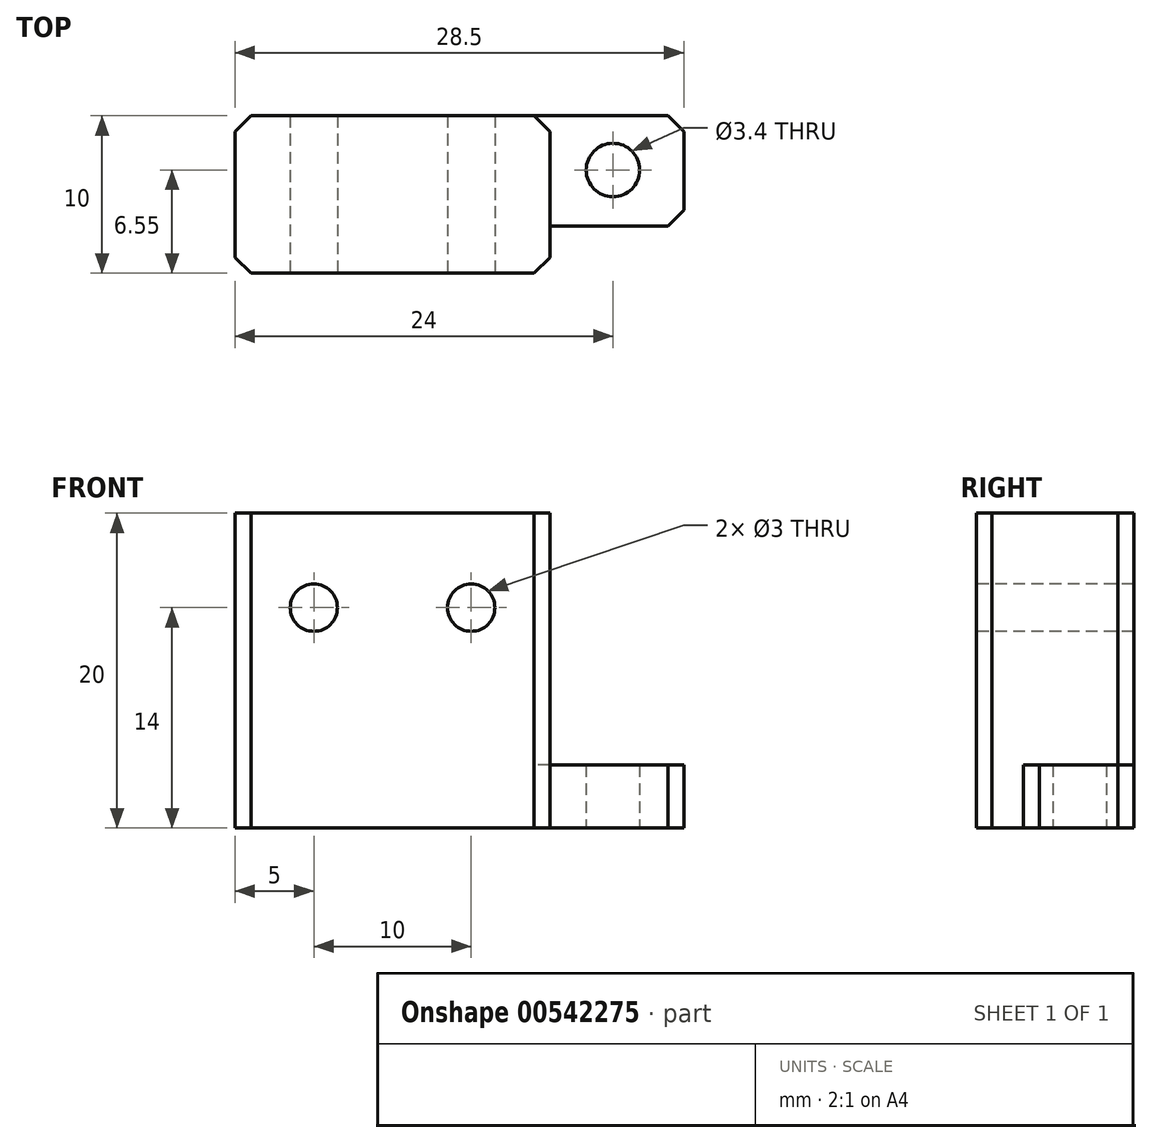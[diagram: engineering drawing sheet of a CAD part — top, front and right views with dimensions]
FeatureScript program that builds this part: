
annotation { "Feature Type Name" : "Feature", "Feature Type Description" : "" }
export const myFeature = defineFeature(function(context is Context, id is Id, definition is map)
    precondition{}
    {
        {
            var Q0;
            Q0=qCreatedBy(makeId("Top.planeOp"),FACE);
            var sketch = newSketch(context, id + "F0", { "sketchPlane" : qUnion([Q0])});
            skLineSegment(sketch, "E0.bottom", {"start": v(-8, 3.45) * mm, "end": v(-4, 3.45) * mm});
            skLineSegment(sketch, "E0.left", {"start": v(-8, 3.45) * mm, "end": v(-8, -3.55) * mm});
            skLineSegment(sketch, "E1.bottom", {"start": v(-8, 3.45) * mm, "end": v(-28, 3.45) * mm});
            skLineSegment(sketch, "E1.right", {"start": v(-28, 3.45) * mm, "end": v(-28, -3.55) * mm});
            skLineSegment(sketch, "E2", {"start": v(-4, 3.45) * mm, "end": v(-4, 0) * mm, "construction": true});
            skCircle(sketch, "E3", {"center": v(-4, 0) * mm, "radius": 1.7 * mm});
            skLineSegment(sketch, "E4", {"start": v(-4, 3.45) * mm, "end": v(0.5, 3.45) * mm});
            skLineSegment(sketch, "E5", {"start": v(-8, -3.55) * mm, "end": v(0.5, -3.55) * mm});
            skLineSegment(sketch, "E6", {"start": v(0.5, 3.45) * mm, "end": v(0.5, -3.55) * mm});
            skLineSegment(sketch, "E7.top", {"start": v(-28, -6.55) * mm, "end": v(-8, -6.55) * mm});
            skLineSegment(sketch, "E7.left", {"start": v(-28, -3.55) * mm, "end": v(-28, -6.55) * mm});
            skLineSegment(sketch, "E7.right", {"start": v(-8, -3.55) * mm, "end": v(-8, -6.55) * mm});
            skSolve(sketch);
        }
        {
            var Q0;
            Q0=makeQuery(id+"F0.imprint","IMPRINT",FACE,{"disambiguationData":[TD([[makeQuery(id+"F0.imprint","IMPRINT",EDGE,{"derivedFrom":sQuery(id+"F0.wireOp",EDGE,"E0.bottom")}),-1.0]])]});
            extrude(context, id + "F1", {"entities" : qUnion([Q0]), "depth" : 4 * mm, "offsetDistance" : 25 * mm});
        }
        {
            var Q0;
            Q0=makeQuery(id+"F0.imprint","IMPRINT",FACE,{"disambiguationData":[TD([[makeQuery(id+"F0.imprint","IMPRINT",EDGE,{"derivedFrom":sQuery(id+"F0.wireOp",EDGE,"E1.bottom")}),1.0]])]});
            extrude(context, id + "F2", {"entities" : qUnion([Q0]), "operationType" : NewBodyOperationType.ADD, "depth" : 20 * mm, "offsetDistance" : 25 * mm});
        }
        {
            var Q0;
            Q0=makeQuery(id+"F2.opExtrude","SWEPT_FACE",FACE,{"disambiguationData":[OSD([sQuery(id+"F0.wireOp",EDGE,"E7.top")])]});
            var sketch = newSketch(context, id + "F3", { "sketchPlane" : qUnion([Q0])});
            skLineSegment(sketch, "E8", {"start": v(-28, 0) * mm, "end": v(-28, 14) * mm, "construction": true});
            skLineSegment(sketch, "E9", {"start": v(-28, 14) * mm, "end": v(-23, 14) * mm, "construction": true});
            skLineSegment(sketch, "E10", {"start": v(-23, 14) * mm, "end": v(-13, 14) * mm, "construction": true});
            skCircle(sketch, "E11", {"center": v(-23, 14) * mm, "radius": 1.5 * mm});
            skCircle(sketch, "E12", {"center": v(-13, 14) * mm, "radius": 1.5 * mm});
            skSolve(sketch);
        }
        {
            var Q0;
            Q0=makeQuery(id+"F3.imprint","IMPRINT",FACE,{"disambiguationData":[TD([[makeQuery(id+"F3.imprint","IMPRINT",EDGE,{"derivedFrom":sQuery(id+"F3.wireOp",EDGE,"E12")}),1.0]])]});
            var Q1;
            Q1=makeQuery(id+"F3.imprint","IMPRINT",FACE,{"disambiguationData":[TD([[makeQuery(id+"F3.imprint","IMPRINT",EDGE,{"derivedFrom":sQuery(id+"F3.wireOp",EDGE,"E11")}),1.0]])]});
            extrude(context, id + "F4", {"entities" : qUnion([Q0, Q1]), "operationType" : NewBodyOperationType.REMOVE, "endBound" : BoundingType.UP_TO_NEXT, "oppositeDirection" : true, "depth" : 25 * mm, "offsetDistance" : 25 * mm});
        }
        {
            var Q0;
            Q0=makeQuery(id+"F2.opExtrude","SWEPT_EDGE",EDGE,{"disambiguationData":[OSD([sQuery(id+"F0.wireOp",EDGE,"E7.top"),sQuery(id+"F0.wireOp",EDGE,"E7.right")])]});
            var Q1;
            Q1=makeQuery(id+"F2.opExtrude","SWEPT_EDGE",EDGE,{"disambiguationData":[OSD([sQuery(id+"F0.wireOp",EDGE,"E7.top"),sQuery(id+"F0.wireOp",EDGE,"E7.left")])]});
            var Q2;
            Q2=makeQuery(id+"F2.opExtrude","SWEPT_EDGE",EDGE,{"disambiguationData":[OSD([sQuery(id+"F0.wireOp",EDGE,"E0.bottom"),sQuery(id+"F0.wireOp",EDGE,"E1.bottom"),sQuery(id+"F0.wireOp",EDGE,"E0.left")])]});
            var Q3;
            Q3=makeQuery(id+"F2.opExtrude","SWEPT_EDGE",EDGE,{"disambiguationData":[OSD([sQuery(id+"F0.wireOp",EDGE,"E1.bottom"),sQuery(id+"F0.wireOp",EDGE,"E1.right")])]});
            var Q4;
            Q4=makeQuery(id+"F1.opExtrude","SWEPT_EDGE",EDGE,{"disambiguationData":[OSD([sQuery(id+"F0.wireOp",EDGE,"E5"),sQuery(id+"F0.wireOp",EDGE,"E6")])]});
            var Q5;
            Q5=makeQuery(id+"F1.opExtrude","SWEPT_EDGE",EDGE,{"disambiguationData":[OSD([sQuery(id+"F0.wireOp",EDGE,"E0.left"),sQuery(id+"F0.wireOp",EDGE,"E5"),sQuery(id+"F0.wireOp",EDGE,"E7.right")])]});
            var Q6;
            Q6=makeQuery(id+"F1.opExtrude","SWEPT_EDGE",EDGE,{"disambiguationData":[OSD([sQuery(id+"F0.wireOp",EDGE,"E4"),sQuery(id+"F0.wireOp",EDGE,"E6")])]});
            chamfer(context, id + "F5", {"entities" : qUnion([Q0, Q1, Q2, Q3, Q4, Q5, Q6]), "width" : 1 * mm, "tangentPropagation" : true});
        }
    });
